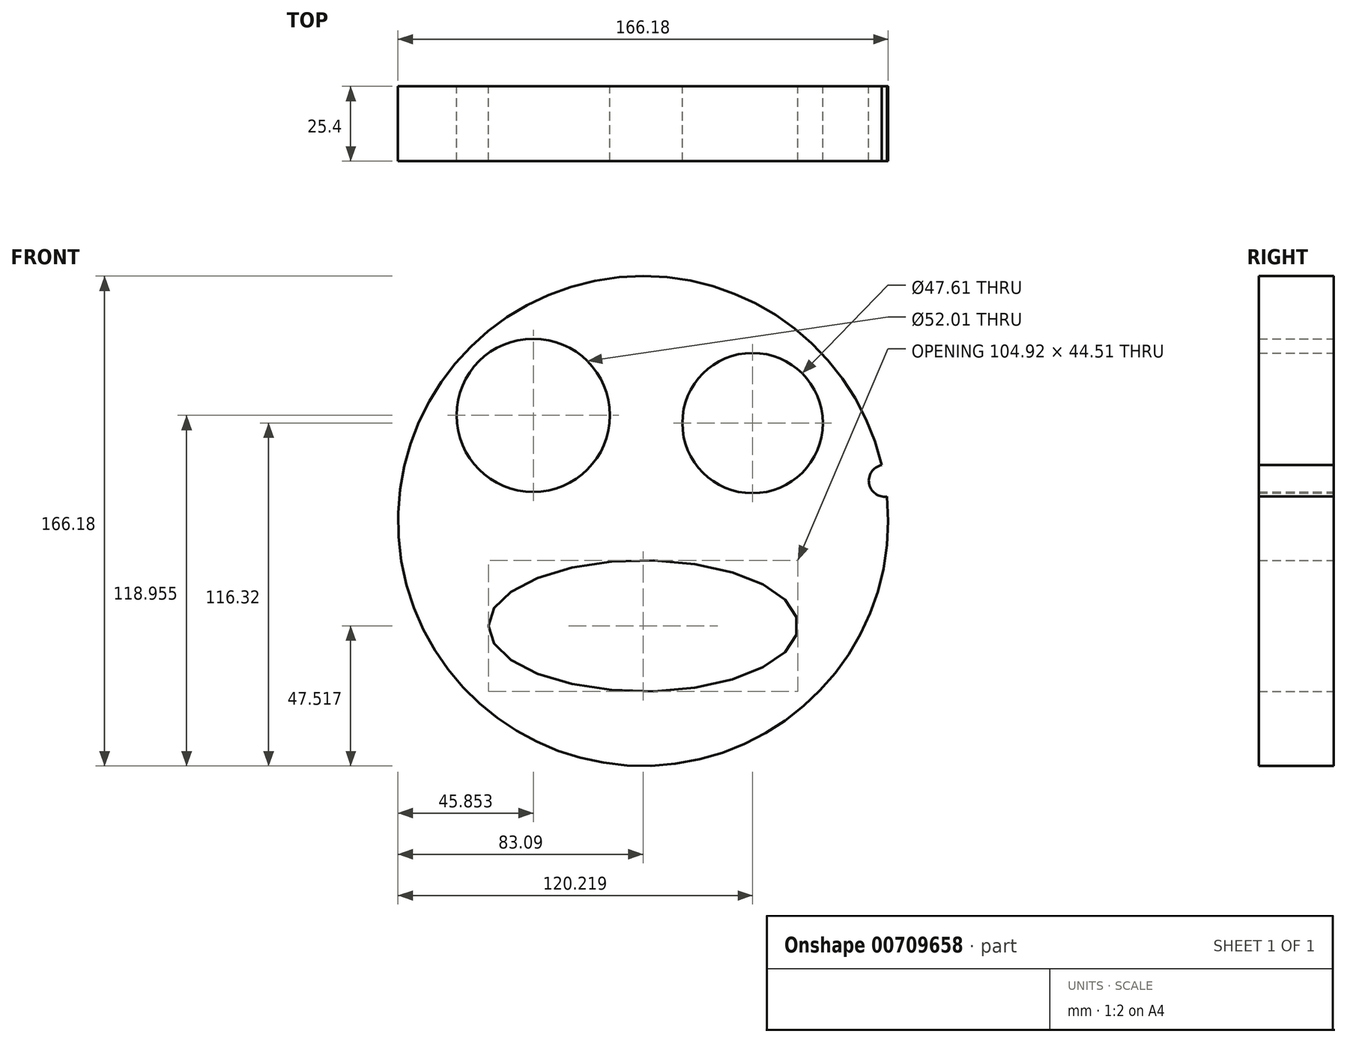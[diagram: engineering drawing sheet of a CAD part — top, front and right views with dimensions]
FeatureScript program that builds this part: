
annotation { "Feature Type Name" : "Feature", "Feature Type Description" : "" }
export const myFeature = defineFeature(function(context is Context, id is Id, definition is map)
    precondition{}
    {
        {
            var Q0;
            Q0=qCreatedBy(makeId("Front.planeOp"),FACE);
            var sketch = newSketch(context, id + "F0", { "sketchPlane" : qUnion([Q0])});
            skCircle(sketch, "E0", {"center": v(0, 0) * mm, "radius": 83.1 * mm});
            skCircle(sketch, "E1", {"center": v(81.96, 13.66) * mm, "radius": 5.41 * mm});
            skSolve(sketch);
        }
        {
            var Q0;
            Q0=qCreatedBy(makeId("Front.planeOp"),FACE);
            var sketch = newSketch(context, id + "F1", { "sketchPlane" : qUnion([Q0])});
            skCircle(sketch, "E2", {"center": v(-37.24, 35.87) * mm, "radius": 26 * mm});
            skCircle(sketch, "E3", {"center": v(37.13, 33.23) * mm, "radius": 23.8 * mm});
            skEllipse(sketch, "E4", {"center": v(0, -35.57) * mm, "majorRadius": 52.46 * mm, "minorRadius": 22.25 * mm, "majorAxis": v(-1, 0)});
            skSolve(sketch);
        }
        {
            var Q0;
            {var subQ0=sQuery(id+"F0.wireOp",EDGE,"E1");var subQ1=sQuery(id+"F0.wireOp",EDGE,"E0");var subQ2=makeQuery(id+"F0.imprint","INTERSECT",VERTEX,{"disambiguationData":[OD(0.0)],"derivedFrom":[subQ1,subQ0]});Q0=makeQuery(id+"F0.imprint","IMPRINT",FACE,{"disambiguationData":[TD([[makeQuery(id+"F0.imprint","IMPRINT",EDGE,{"disambiguationData":[TD([[subQ2,1.0]])],"derivedFrom":subQ1}),1.0]])]});}
            extrude(context, id + "F2", {"entities" : qUnion([Q0]), "depth" : 25.4 * mm, "offsetDistance" : 25.4 * mm});
        }
        {
            var Q0;
            Q0=makeQuery(id+"F1.imprint","IMPRINT",FACE,{"disambiguationData":[TD([[makeQuery(id+"F1.imprint","IMPRINT",EDGE,{"derivedFrom":sQuery(id+"F1.wireOp",EDGE,"E3")}),1.0]])]});
            var Q1;
            Q1=makeQuery(id+"F1.imprint","IMPRINT",FACE,{"disambiguationData":[TD([[makeQuery(id+"F1.imprint","IMPRINT",EDGE,{"derivedFrom":sQuery(id+"F1.wireOp",EDGE,"E2")}),1.0]])]});
            var Q2;
            Q2=makeQuery(id+"F1.imprint","IMPRINT",FACE,{"disambiguationData":[TD([[makeQuery(id+"F1.imprint","IMPRINT",EDGE,{"derivedFrom":sQuery(id+"F1.wireOp",EDGE,"E4")}),1.0]])]});
            extrude(context, id + "F3", {"entities" : qUnion([Q0, Q1, Q2]), "operationType" : NewBodyOperationType.REMOVE, "depth" : 51.56 * mm, "offsetDistance" : 25.4 * mm});
        }
    });
